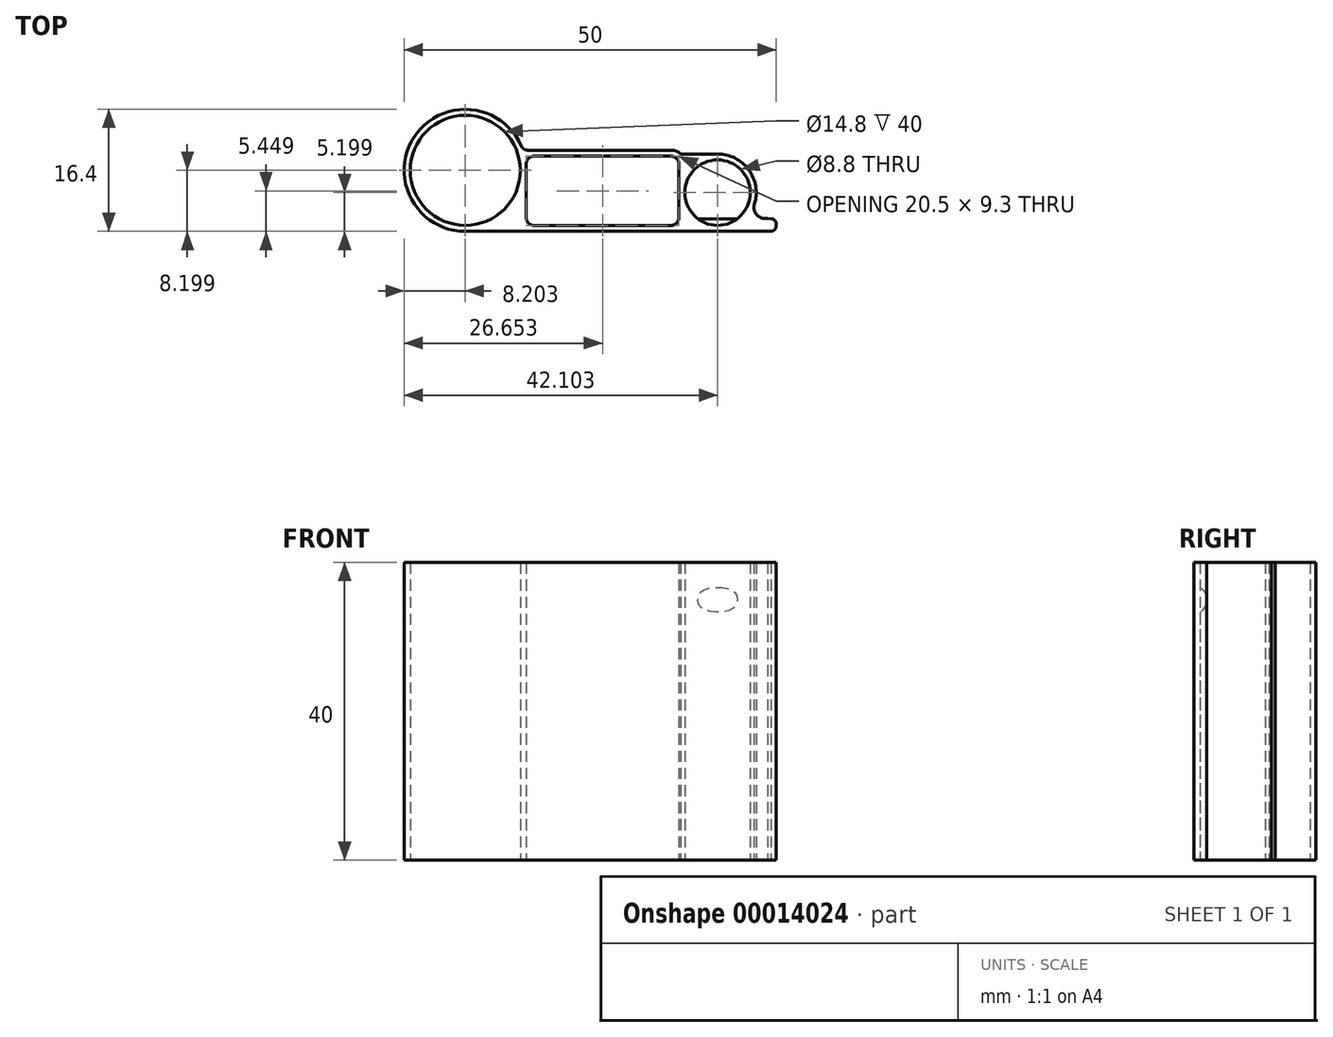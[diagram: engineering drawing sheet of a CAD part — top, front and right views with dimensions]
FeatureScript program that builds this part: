
annotation { "Feature Type Name" : "Feature", "Feature Type Description" : "" }
export const myFeature = defineFeature(function(context is Context, id is Id, definition is map)
    precondition{}
    {
        {
            var Q0;
            Q0=qCreatedBy(makeId("Top.planeOp"),FACE);
            var sketch = newSketch(context, id + "F0", { "sketchPlane" : qUnion([Q0])});
            skCircle(sketch, "E0", {"center": v(-31.66, -11.88) * mm, "radius": 7.4 * mm});
            skLineSegment(sketch, "E1.0", {"start": v(-31.66, -20.08) * mm, "end": v(9.34, -20.08) * mm});
            skArc(sketch, "E2.trimOffspring", {"start": v(-24.15, -8.58) * mm, "mid": v(-38.52, -7.4) * mm, "end": v(-31.66, -20.08) * mm});
            skLineSegment(sketch, "E3.trimOffspring", {"start": v(8.64, -18.37) * mm, "end": v(8.97, -18.37) * mm});
            skPoint(sketch, "E4.end.orphan", {"position": v(-39.86, -11.88) * mm});
            skPoint(sketch, "E5.visualSharp", {"position": v(10.14, -18.37) * mm});
            skPoint(sketch, "E6.visualSharp", {"position": v(10.14, -20.08) * mm});
            skPoint(sketch, "E7.visualSharp", {"position": v(-1.3, -18.37) * mm});
            skLineSegment(sketch, "E8", {"start": v(10.14, -19.17) * mm, "end": v(10.14, -19.28) * mm});
            skArc(sketch, "E9.filletArc", {"start": v(10.14, -19.17) * mm, "mid": v(9.94, -18.64) * mm, "end": v(9.43, -18.38) * mm});
            skArc(sketch, "E10.filletArc", {"start": v(9.34, -20.08) * mm, "mid": v(9.9, -19.85) * mm, "end": v(10.14, -19.28) * mm});
            skLineSegment(sketch, "E11", {"start": v(-23.46, -18.28) * mm, "end": v(-23.46, -10.98) * mm});
            skLineSegment(sketch, "E12", {"start": v(-22.46, -19.28) * mm, "end": v(-3.96, -19.28) * mm});
            skLineSegment(sketch, "E13", {"start": v(-22.46, -9.98) * mm, "end": v(-3.96, -9.98) * mm});
            skLineSegment(sketch, "E14.trimOffspring", {"start": v(-2.96, -10.98) * mm, "end": v(-2.96, -18.28) * mm});
            skCircle(sketch, "E15", {"center": v(2.24, -14.88) * mm, "radius": 4.4 * mm});
            skArc(sketch, "E16", {"start": v(7.2, -16.43) * mm, "mid": v(6.43, -11.8) * mm, "end": v(2.24, -9.68) * mm});
            skPoint(sketch, "E17.visualSharp", {"position": v(-23.82, -9.48) * mm});
            skPoint(sketch, "E18.visualSharp", {"position": v(9.34, -18.37) * mm});
            skPoint(sketch, "E19.visualSharp", {"position": v(6.1, -18.37) * mm});
            skArc(sketch, "E19.filletArc", {"start": v(7.2, -16.43) * mm, "mid": v(7.43, -17.76) * mm, "end": v(8.64, -18.37) * mm});
            skLineSegment(sketch, "E20", {"start": v(9.43, -18.38) * mm, "end": v(8.97, -18.37) * mm});
            skPoint(sketch, "E21.visualSharp", {"position": v(-23.46, -9.98) * mm});
            skArc(sketch, "E21.filletArc", {"start": v(-22.46, -9.98) * mm, "mid": v(-23.16, -10.27) * mm, "end": v(-23.46, -10.98) * mm});
            skPoint(sketch, "E22.visualSharp", {"position": v(-23.46, -19.28) * mm});
            skArc(sketch, "E22.filletArc", {"start": v(-23.46, -18.28) * mm, "mid": v(-23.16, -18.99) * mm, "end": v(-22.46, -19.28) * mm});
            skPoint(sketch, "E23.visualSharp", {"position": v(-2.96, -9.98) * mm});
            skArc(sketch, "E23.filletArc", {"start": v(-2.96, -10.98) * mm, "mid": v(-3.25, -10.27) * mm, "end": v(-3.96, -9.98) * mm});
            skPoint(sketch, "E24.visualSharp", {"position": v(-2.96, -19.28) * mm});
            skArc(sketch, "E24.filletArc", {"start": v(-3.96, -19.28) * mm, "mid": v(-3.25, -18.99) * mm, "end": v(-2.96, -18.28) * mm});
            skLineSegment(sketch, "E25.0", {"start": v(-23.23, -9.18) * mm, "end": v(-3.96, -9.18) * mm});
            skPoint(sketch, "E26.visualSharp", {"position": v(-23.91, -9.18) * mm});
            skArc(sketch, "E26.filletArc", {"start": v(-24.15, -8.58) * mm, "mid": v(-23.78, -9.02) * mm, "end": v(-23.23, -9.18) * mm});
            skArc(sketch, "E27.0", {"start": v(-2.71, -9.68) * mm, "mid": v(-3.29, -9.31) * mm, "end": v(-3.96, -9.18) * mm});
            skLineSegment(sketch, "E28", {"start": v(2.24, -9.68) * mm, "end": v(-2.71, -9.68) * mm});
            skSolve(sketch);
        }
        {
            var Q0;
            Q0=makeQuery(id+"F0.imprint","IMPRINT",FACE,{"disambiguationData":[TD([[makeQuery(id+"F0.imprint","IMPRINT",EDGE,{"derivedFrom":sQuery(id+"F0.wireOp",EDGE,"E0")}),-1.0]])]});
            var Q1;
            Q1=qSketchRegion(id+"F0",true);
            extrude(context, id + "F1", {"entities" : qUnion([Q0, Q1]), "depth" : 40 * mm});
        }
        {
            var Q0;
            Q0=qCreatedBy(makeId("Right.planeOp"),FACE);
            cPlane(context, id + "F2", {"entities" : qUnion([Q0]), "cplaneType" : CPlaneType.OFFSET, "offset" : 7 * mm, "width" : 150 * mm, "height" : 150 * mm});
        }
        {
            var Q0;
            Q0=qCreatedBy(id+"F2.planeOp",FACE);
            var sketch = newSketch(context, id + "F3", { "sketchPlane" : qUnion([Q0])});
            skArc(sketch, "E29", {"start": v(-19.58, 33.17) * mm, "mid": v(-18.38, 35) * mm, "end": v(-19.58, 36.83) * mm});
            skLineSegment(sketch, "E30", {"start": v(-20.38, 35) * mm, "end": v(-18.38, 35) * mm});
            skLineSegment(sketch, "E31", {"start": v(-19.58, 36.83) * mm, "end": v(-19.58, 33.17) * mm});
            skSolve(sketch);
        }
        {
            var Q0;
            Q0=qSketchRegion(id+"F3",true);
            extrude(context, id + "F4", {"entities" : qUnion([Q0]), "operationType" : NewBodyOperationType.ADD, "oppositeDirection" : true, "depth" : 9 * mm});
        }
    });
